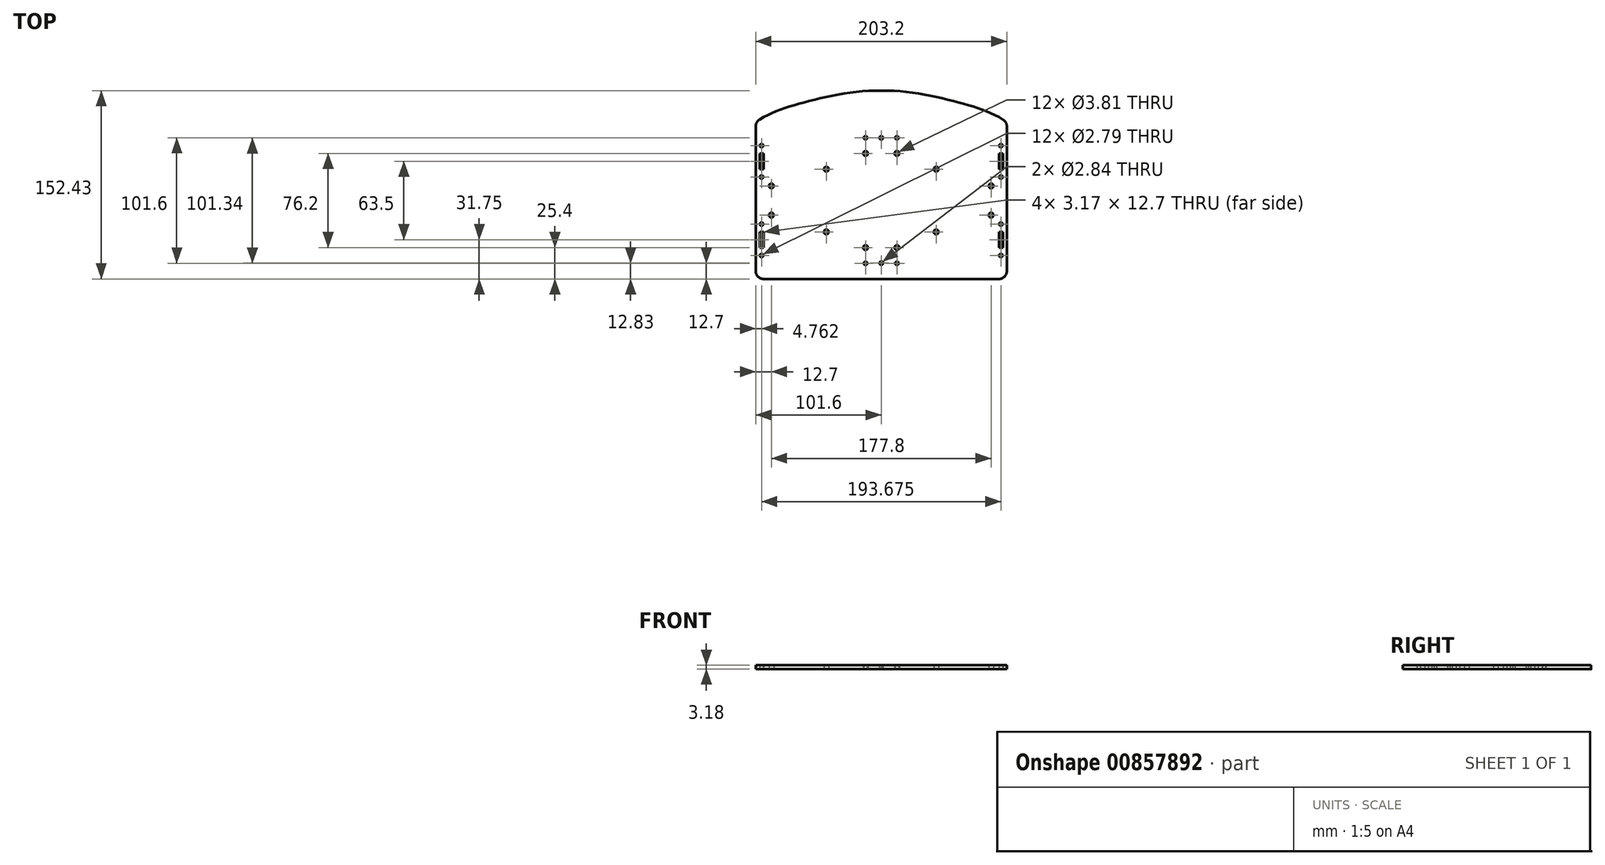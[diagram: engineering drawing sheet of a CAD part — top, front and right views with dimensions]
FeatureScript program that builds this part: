
annotation { "Feature Type Name" : "Feature", "Feature Type Description" : "" }
export const myFeature = defineFeature(function(context is Context, id is Id, definition is map)
    precondition{}
    {
        {
            var Q0;
            Q0=qCreatedBy(makeId("Top.planeOp"),FACE);
            var sketch = newSketch(context, id + "F0", { "sketchPlane" : qUnion([Q0])});
            skLineSegment(sketch, "E0.bottom", {"start": v(95.25, -63.5) * mm, "end": v(-95.25, -63.5) * mm});
            skLineSegment(sketch, "E0.left", {"start": v(101.6, -57.15) * mm, "end": v(101.6, 60.03) * mm});
            skLineSegment(sketch, "E0.right", {"start": v(-101.6, -57.15) * mm, "end": v(-101.6, 60.03) * mm});
            skPoint(sketch, "E0.middle", {"position": v(0, 0) * mm});
            skLineSegment(sketch, "E1", {"start": v(0, 0) * mm, "end": v(0, 49.25) * mm});
            skPoint(sketch, "E1.endSnap0", {"position": v(0, 63.5) * mm});
            skFitSpline(sketch, "E2", {"points": [v(0, 88.9) * mm, v(63.7, 79.05) * mm, v(101.6, 63.5) * mm], "startDerivative": vector(120.27, 2.72) * mm, "endDerivative": vector(82.07, -54.82) * mm});
            skFitSpline(sketch, "E3.MirrorCS", {"points": [v(0, 88.9) * mm, v(-63.7, 79.05) * mm, v(-101.6, 63.5) * mm], "startDerivative": vector(-120.27, 2.72) * mm, "endDerivative": vector(-82.07, -54.82) * mm});
            skArc(sketch, "E4.filletArc", {"start": v(-98.57, 65.44) * mm, "mid": v(-100.8, 63.13) * mm, "end": v(-101.6, 60.03) * mm});
            skArc(sketch, "E5.filletArc", {"start": v(101.6, 60.03) * mm, "mid": v(100.8, 63.13) * mm, "end": v(98.57, 65.44) * mm});
            skLineSegment(sketch, "E6", {"start": v(0, 0) * mm, "end": v(155.86, 0) * mm});
            skPoint(sketch, "E7.visualSharp", {"position": v(101.6, -63.5) * mm});
            skArc(sketch, "E7.filletArc", {"start": v(95.25, -63.5) * mm, "mid": v(99.74, -61.64) * mm, "end": v(101.6, -57.15) * mm});
            skPoint(sketch, "E8.visualSharp", {"position": v(-101.6, -63.5) * mm});
            skArc(sketch, "E8.filletArc", {"start": v(-101.6, -57.15) * mm, "mid": v(-99.74, -61.64) * mm, "end": v(-95.25, -63.5) * mm});
            skCircle(sketch, "E9", {"center": v(88.9, 11.81) * mm, "radius": 1.9 * mm});
            skCircle(sketch, "E10.MirrorC", {"center": v(88.9, -11.81) * mm, "radius": 1.9 * mm});
            skCircle(sketch, "E11.MirrorC", {"center": v(-88.9, 11.81) * mm, "radius": 1.9 * mm});
            skCircle(sketch, "E12.MirrorC", {"center": v(-88.9, -11.81) * mm, "radius": 1.9 * mm});
            skCircle(sketch, "E13", {"center": v(44.45, 25.4) * mm, "radius": 1.9 * mm});
            skCircle(sketch, "E14.MirrorC", {"center": v(44.45, -25.4) * mm, "radius": 1.9 * mm});
            skCircle(sketch, "E15.MirrorC", {"center": v(-44.45, 25.4) * mm, "radius": 1.9 * mm});
            skCircle(sketch, "E16.MirrorC", {"center": v(-44.45, -25.4) * mm, "radius": 1.9 * mm});
            skLineSegment(sketch, "E17.bottom", {"start": v(95.25, -25.4) * mm, "end": v(98.43, -25.4) * mm});
            skLineSegment(sketch, "E17.top", {"start": v(95.25, -38.1) * mm, "end": v(98.43, -38.1) * mm});
            skLineSegment(sketch, "E17.left", {"start": v(95.25, -25.4) * mm, "end": v(95.25, -38.1) * mm});
            skLineSegment(sketch, "E17.right", {"start": v(98.43, -25.4) * mm, "end": v(98.43, -38.1) * mm});
            skCircle(sketch, "E18", {"center": v(96.84, -19.05) * mm, "radius": 1.4 * mm});
            skPoint(sketch, "E19", {"position": v(96.84, -25.4) * mm});
            skPoint(sketch, "E20", {"position": v(96.84, -38.1) * mm});
            skCircle(sketch, "E21", {"center": v(96.84, -44.45) * mm, "radius": 1.4 * mm});
            skCircle(sketch, "E22.MirrorC", {"center": v(96.84, 19.05) * mm, "radius": 1.4 * mm});
            skLineSegment(sketch, "E23.MirrorCS", {"start": v(95.25, 25.4) * mm, "end": v(95.25, 38.1) * mm});
            skLineSegment(sketch, "E24.MirrorCS", {"start": v(95.25, 25.4) * mm, "end": v(98.43, 25.4) * mm});
            skLineSegment(sketch, "E25.MirrorCS", {"start": v(98.43, 25.4) * mm, "end": v(98.43, 38.1) * mm});
            skLineSegment(sketch, "E26.MirrorCS", {"start": v(95.25, 38.1) * mm, "end": v(98.43, 38.1) * mm});
            skPoint(sketch, "E27.MirrorP", {"position": v(96.84, 38.1) * mm});
            skPoint(sketch, "E28.MirrorP", {"position": v(96.84, 25.4) * mm});
            skCircle(sketch, "E29.MirrorC", {"center": v(96.84, 44.45) * mm, "radius": 1.4 * mm});
            skCircle(sketch, "E30.MirrorC", {"center": v(-96.84, 44.45) * mm, "radius": 1.4 * mm});
            skLineSegment(sketch, "E31.MirrorCS", {"start": v(-95.25, 38.1) * mm, "end": v(-98.43, 38.1) * mm});
            skPoint(sketch, "E32.MirrorP", {"position": v(-96.84, 38.1) * mm});
            skLineSegment(sketch, "E33.MirrorCS", {"start": v(-98.43, 25.4) * mm, "end": v(-98.43, 38.1) * mm});
            skLineSegment(sketch, "E34.MirrorCS", {"start": v(-95.25, 25.4) * mm, "end": v(-95.25, 38.1) * mm});
            skPoint(sketch, "E35.MirrorP", {"position": v(-96.84, 25.4) * mm});
            skLineSegment(sketch, "E36.MirrorCS", {"start": v(-95.25, 25.4) * mm, "end": v(-98.43, 25.4) * mm});
            skCircle(sketch, "E37.MirrorC", {"center": v(-96.84, 19.05) * mm, "radius": 1.4 * mm});
            skCircle(sketch, "E38.MirrorC", {"center": v(-96.84, -19.05) * mm, "radius": 1.4 * mm});
            skLineSegment(sketch, "E39.MirrorCS", {"start": v(-95.25, -25.4) * mm, "end": v(-98.43, -25.4) * mm});
            skPoint(sketch, "E40.MirrorP", {"position": v(-96.84, -25.4) * mm});
            skLineSegment(sketch, "E41.MirrorCS", {"start": v(-98.43, -25.4) * mm, "end": v(-98.43, -38.1) * mm});
            skLineSegment(sketch, "E42.MirrorCS", {"start": v(-95.25, -25.4) * mm, "end": v(-95.25, -38.1) * mm});
            skLineSegment(sketch, "E43.MirrorCS", {"start": v(-95.25, -38.1) * mm, "end": v(-98.43, -38.1) * mm});
            skPoint(sketch, "E44.MirrorP", {"position": v(-96.84, -38.1) * mm});
            skCircle(sketch, "E45.MirrorC", {"center": v(-96.84, -44.45) * mm, "radius": 1.4 * mm});
            skCircle(sketch, "E46", {"center": v(12.7, -50.8) * mm, "radius": 1.4 * mm});
            skCircle(sketch, "E47", {"center": v(12.7, -38.1) * mm, "radius": 1.9 * mm});
            skCircle(sketch, "E48.MirrorC", {"center": v(-12.7, -38.1) * mm, "radius": 1.9 * mm});
            skCircle(sketch, "E49.MirrorC", {"center": v(-12.7, -50.8) * mm, "radius": 1.4 * mm});
            skCircle(sketch, "E50", {"center": v(0, -50.67) * mm, "radius": 1.42 * mm});
            skCircle(sketch, "E51.MirrorC", {"center": v(12.7, 50.8) * mm, "radius": 1.4 * mm});
            skCircle(sketch, "E52.MirrorC", {"center": v(12.7, 38.1) * mm, "radius": 1.9 * mm});
            skCircle(sketch, "E53.MirrorC", {"center": v(-12.7, 50.8) * mm, "radius": 1.4 * mm});
            skCircle(sketch, "E54.MirrorC", {"center": v(-12.7, 38.1) * mm, "radius": 1.9 * mm});
            skCircle(sketch, "E55.MirrorC", {"center": v(0, 50.67) * mm, "radius": 1.42 * mm});
            skLineSegment(sketch, "E56.trimOffspring", {"start": v(0, 52.1) * mm, "end": v(0, 88.9) * mm});
            skSolve(sketch);
        }
        {
            var Q0;
            Q0=makeQuery(id+"F0.imprint","IMPRINT",FACE,{"disambiguationData":[TD([[makeQuery(id+"F0.imprint","IMPRINT",EDGE,{"derivedFrom":sQuery(id+"F0.wireOp",EDGE,"E0.bottom")}),-1.0]])]});
            var Q1;
            {var subQ1=sQuery(id+"F0.wireOp",EDGE,"E1");Q1=makeQuery(id+"F0.imprint","IMPRINT",FACE,{"disambiguationData":[TD([[makeQuery(id+"F0.imprint","IMPRINT",EDGE,{"derivedFrom":subQ1}),-1.0]])]});}
            extrude(context, id + "F1", {"entities" : qUnion([Q0, Q1]), "depth" : 3.17 * mm, "offsetDistance" : 25.4 * mm});
        }
    });
